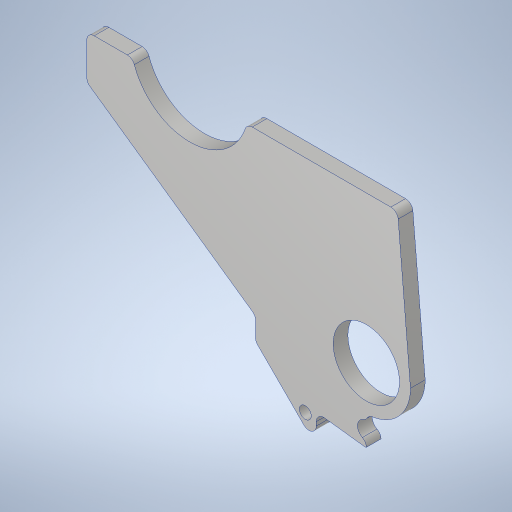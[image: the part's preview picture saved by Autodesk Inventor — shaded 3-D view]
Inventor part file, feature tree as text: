
AUTODESK INVENTOR PART (.ipt)
format: ipt  version: 2023.4 (Build 274418000, 418)  size: 338,432 bytes
history: native  units: in
note: dims shown in document units (in); Inventor stores cm internally (conversion verified against a paired STEP export)
features: fillet x3, sketch x1, extrude x1, chamfer x1, hole x1
ambient origin geometry x8: Origin, YZ Plane, XZ Plane, XY Plane, X Axis, Y Axis, Z Axis, Center Point
bodies: Solid1 (feature_tree)
feature tree (7):
  sketch  "Sketch1"  dims[d0=4.0in d1=5.5in d3=2.0in d4=0.25in d6=0.75in d7=1.5in d8=1.5in d9=1.125in d10=0.8589in d11=1.25in d12=3.5in d15=0.35in d18=0.6528in d19=0.25in d20=0.0in d21=0.125in d25=0.3in d26=1.0in d28=0.1875in d31=0.25in d33=0.85in d34=0.875in d35=0.125in d36=45.0deg d37=0.125in d38=3.0in d39=0.125in d40=0.25in d42=0.201in d43=0.75in d44=0.385in d45=0.25in d46=0.5635in d47=1.0in d48=0.8108in d49=0.375in]
  extrude  "Extrusion1"  Depth=1.0in
  fillet  "Fillet1"  Radius=2.0in
  chamfer  "Chamfer1"  Distance=0.25in
  fillet  "Fillet3"  Radius=0.75in
  fillet  "Fillet4"  Radius=1.5in
  hole  "Hole1"  [1 undecoded]
note: 1 required parameter value undecoded (feature->parameter linkage not recoverable at this tier; creation-order binding heuristic only, values carry confidence <= 0.55)
